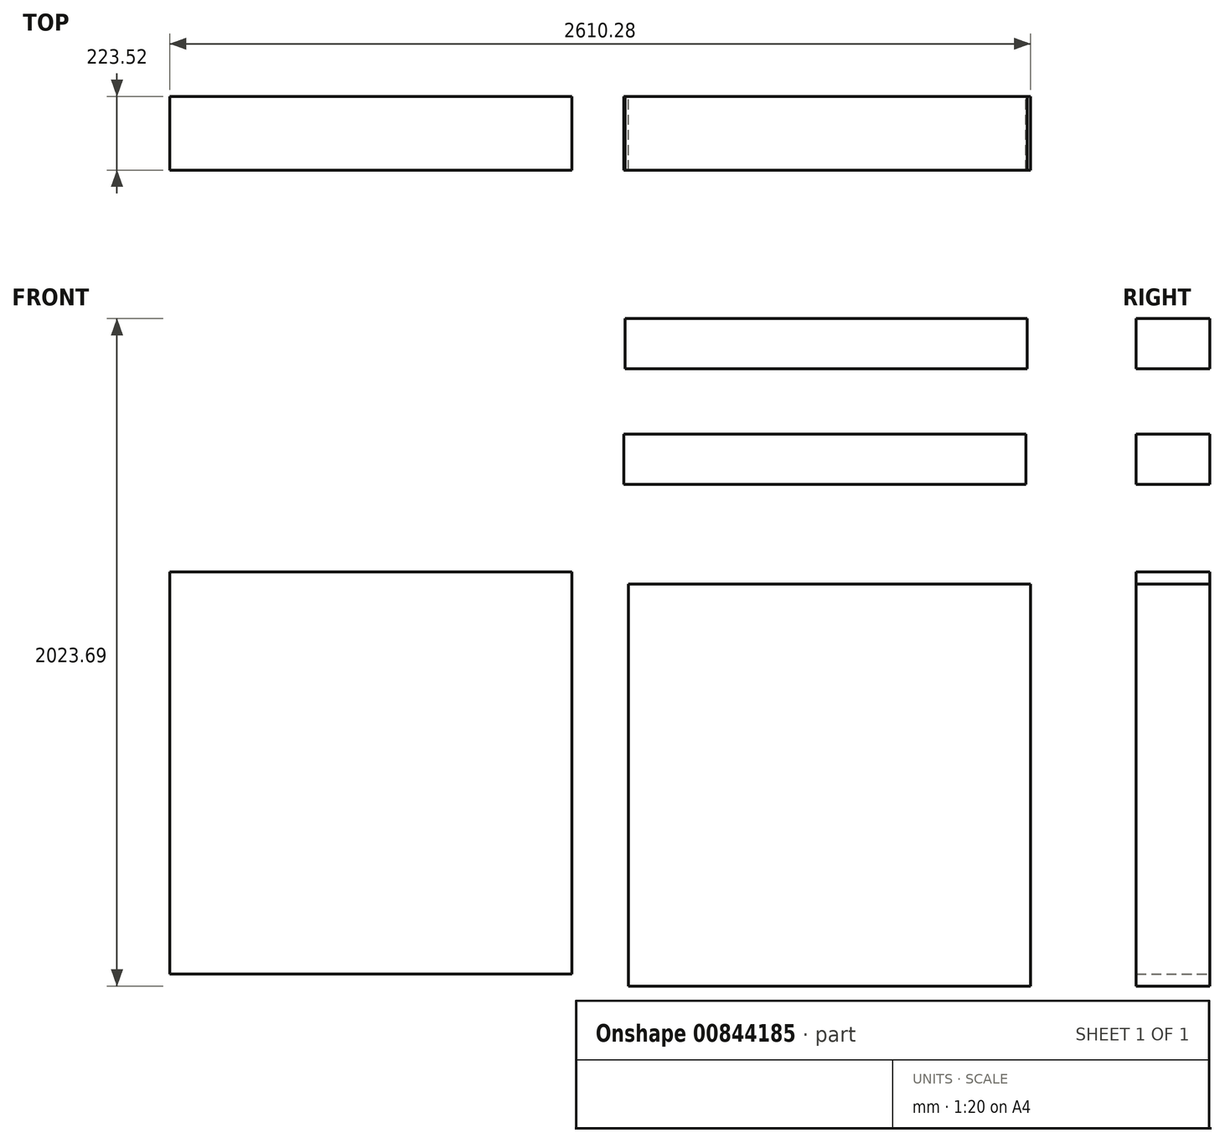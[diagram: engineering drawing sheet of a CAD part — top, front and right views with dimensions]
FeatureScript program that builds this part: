
annotation { "Feature Type Name" : "Feature", "Feature Type Description" : "" }
export const myFeature = defineFeature(function(context is Context, id is Id, definition is map)
    precondition{}
    {
        {
            var Q0;
            Q0=qCreatedBy(makeId("Front.planeOp"),FACE);
            var sketch = newSketch(context, id + "F0", { "sketchPlane" : qUnion([Q0])});
            skLineSegment(sketch, "E0.bottom", {"start": v(-631.22, 726.35) * mm, "end": v(587.98, 726.35) * mm});
            skLineSegment(sketch, "E0.top", {"start": v(-631.22, -492.85) * mm, "end": v(587.98, -492.85) * mm});
            skLineSegment(sketch, "E0.left", {"start": v(-631.22, 726.35) * mm, "end": v(-631.22, -492.85) * mm});
            skLineSegment(sketch, "E0.right", {"start": v(587.98, 726.35) * mm, "end": v(587.98, -492.85) * mm});
            skSolve(sketch);
        }
        {
            var Q0;
            Q0=qCreatedBy(makeId("Front.planeOp"),FACE);
            var sketch = newSketch(context, id + "F1", { "sketchPlane" : qUnion([Q0])});
            skLineSegment(sketch, "E1.bottom", {"start": v(749.23, 1494.02) * mm, "end": v(1968.43, 1494.02) * mm});
            skLineSegment(sketch, "E1.top", {"start": v(749.23, 1341.62) * mm, "end": v(1968.43, 1341.62) * mm});
            skLineSegment(sketch, "E1.left", {"start": v(749.23, 1494.02) * mm, "end": v(749.23, 1341.62) * mm});
            skLineSegment(sketch, "E1.right", {"start": v(1968.43, 1494.02) * mm, "end": v(1968.43, 1341.62) * mm});
            skSolve(sketch);
        }
        {
            var Q0;
            Q0=qCreatedBy(makeId("Front.planeOp"),FACE);
            var sketch = newSketch(context, id + "F2", { "sketchPlane" : qUnion([Q0])});
            skLineSegment(sketch, "E2.bottom", {"start": v(745.17, 1143.94) * mm, "end": v(1964.37, 1143.94) * mm});
            skLineSegment(sketch, "E2.top", {"start": v(745.17, 991.54) * mm, "end": v(1964.37, 991.54) * mm});
            skLineSegment(sketch, "E2.left", {"start": v(745.17, 1143.94) * mm, "end": v(745.17, 991.54) * mm});
            skLineSegment(sketch, "E2.right", {"start": v(1964.37, 1143.94) * mm, "end": v(1964.37, 991.54) * mm});
            skSolve(sketch);
        }
        {
            var Q0;
            Q0=qCreatedBy(makeId("Front.planeOp"),FACE);
            var sketch = newSketch(context, id + "F3", { "sketchPlane" : qUnion([Q0])});
            skLineSegment(sketch, "E3.bottom", {"start": v(759.86, 689.53) * mm, "end": v(1979.06, 689.53) * mm});
            skLineSegment(sketch, "E3.top", {"start": v(759.86, -529.67) * mm, "end": v(1979.06, -529.67) * mm});
            skLineSegment(sketch, "E3.left", {"start": v(759.86, 689.53) * mm, "end": v(759.86, -529.67) * mm});
            skLineSegment(sketch, "E3.right", {"start": v(1979.06, 689.53) * mm, "end": v(1979.06, -529.67) * mm});
            skSolve(sketch);
        }
        {
            var Q0;
            Q0=makeQuery(id+"F0.imprint","IMPRINT",FACE,{"disambiguationData":[TD([[makeQuery(id+"F0.imprint","IMPRINT",EDGE,{"derivedFrom":sQuery(id+"F0.wireOp",EDGE,"E0.bottom")}),-1.0]])]});
            var Q1;
            Q1=makeQuery(id+"F3.imprint","IMPRINT",FACE,{"disambiguationData":[TD([[makeQuery(id+"F3.imprint","IMPRINT",EDGE,{"derivedFrom":sQuery(id+"F3.wireOp",EDGE,"E3.bottom")}),-1.0]])]});
            var Q2;
            Q2=makeQuery(id+"F2.imprint","IMPRINT",FACE,{"disambiguationData":[TD([[makeQuery(id+"F2.imprint","IMPRINT",EDGE,{"derivedFrom":sQuery(id+"F2.wireOp",EDGE,"E2.bottom")}),-1.0]])]});
            var Q3;
            Q3=makeQuery(id+"F1.imprint","IMPRINT",FACE,{"disambiguationData":[TD([[makeQuery(id+"F1.imprint","IMPRINT",EDGE,{"derivedFrom":sQuery(id+"F1.wireOp",EDGE,"E1.bottom")}),-1.0]])]});
            extrude(context, id + "F4", {"entities" : qUnion([Q0, Q1, Q2, Q3]), "depth" : 223.52 * mm, "offsetDistance" : 25.4 * mm});
        }
    });
